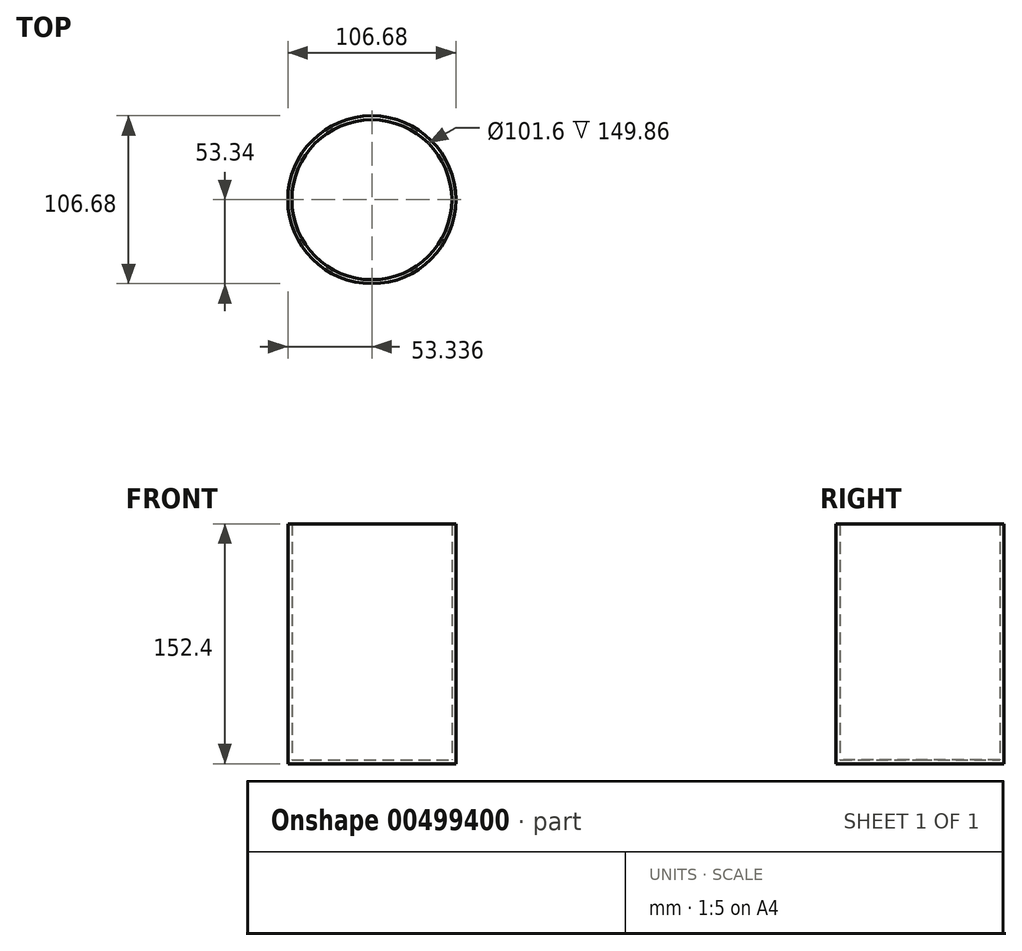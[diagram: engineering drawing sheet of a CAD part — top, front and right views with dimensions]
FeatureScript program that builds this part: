
annotation { "Feature Type Name" : "Feature", "Feature Type Description" : "" }
export const myFeature = defineFeature(function(context is Context, id is Id, definition is map)
    precondition{}
    {
        {
            var Q0;
            Q0=qCreatedBy(makeId("Front.planeOp"),FACE);
            var sketch = newSketch(context, id + "F0", { "sketchPlane" : qUnion([Q0])});
            skLineSegment(sketch, "E0.bottom", {"start": v(2.98, 0) * mm, "end": v(53.78, 0) * mm});
            skLineSegment(sketch, "E0.top", {"start": v(2.98, 152.4) * mm, "end": v(53.78, 152.4) * mm});
            skLineSegment(sketch, "E0.left", {"start": v(2.98, 0) * mm, "end": v(2.98, 152.4) * mm});
            skLineSegment(sketch, "E0.right", {"start": v(53.78, 0) * mm, "end": v(53.78, 152.4) * mm});
            skLineSegment(sketch, "E1.bottom", {"start": v(53.78, 0) * mm, "end": v(56.32, 0) * mm});
            skLineSegment(sketch, "E1.top", {"start": v(53.78, 152.4) * mm, "end": v(56.32, 152.4) * mm});
            skLineSegment(sketch, "E1.right", {"start": v(56.32, 0) * mm, "end": v(56.32, 152.4) * mm});
            skSolve(sketch);
        }
        {
            var Q0;
            Q0=makeQuery(id+"F0.imprint","IMPRINT",FACE,{"disambiguationData":[TD([[makeQuery(id+"F0.imprint","IMPRINT",EDGE,{"derivedFrom":sQuery(id+"F0.wireOp",EDGE,"E0.bottom")}),1.0]])]});
            var Q1;
            Q1=makeQuery(id+"F0.imprint","IMPRINT",FACE,{"disambiguationData":[TD([[makeQuery(id+"F0.imprint","IMPRINT",EDGE,{"derivedFrom":sQuery(id+"F0.wireOp",EDGE,"E1.bottom")}),1.0]])]});
            var Q2;
            Q2=sQuery(id+"F0.wireOp",EDGE,"E0.left");
            revolve(context, id + "F1", {"entities" : qUnion([Q0, Q1]), "axis" : qUnion([Q2]), "revolveType" : RevolveType.FULL});
        }
        {
            var Q0;
            Q0=makeQuery(id+"F1.opRevolve","SWEPT_FACE",FACE,{"disambiguationData":[OSD([sQuery(id+"F0.wireOp",EDGE,"E0.top"),sQuery(id+"F0.wireOp",EDGE,"E1.top")])]});
            var Q1;
            Q1=makeQuery(id+"F1.opRevolve","SWEPT_BODY",BODY,{"disambiguationData":[OSD([sQuery(id+"F0.wireOp",EDGE,"E0.bottom"),sQuery(id+"F0.wireOp",EDGE,"E0.top"),sQuery(id+"F0.wireOp",EDGE,"E0.left"),sQuery(id+"F0.wireOp",EDGE,"E1.bottom"),sQuery(id+"F0.wireOp",EDGE,"E1.top"),sQuery(id+"F0.wireOp",EDGE,"E1.right")])]});
            shell(context, id + "F2", {"entities" : qUnion([Q0]), "parts" : qUnion([Q1]), "thickness" : 2.54 * mm});
        }
    });
